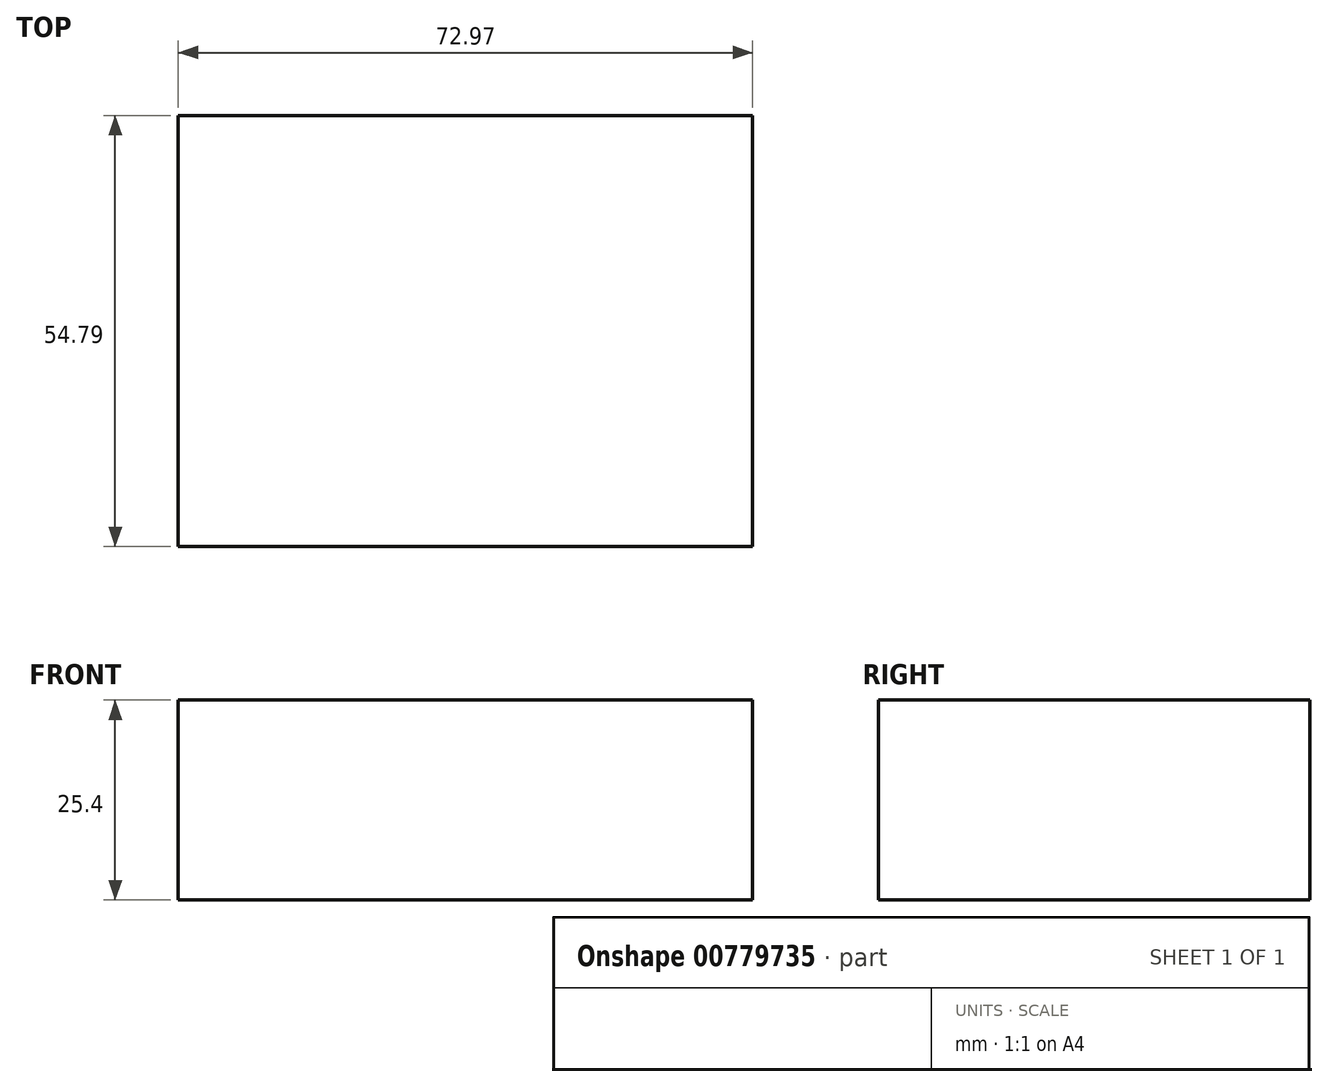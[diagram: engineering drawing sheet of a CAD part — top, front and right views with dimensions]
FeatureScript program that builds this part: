
annotation { "Feature Type Name" : "Feature", "Feature Type Description" : "" }
export const myFeature = defineFeature(function(context is Context, id is Id, definition is map)
    precondition{}
    {
        {
            var Q0;
            Q0=qCreatedBy(makeId("Top.planeOp"),FACE);
            var sketch = newSketch(context, id + "F0", { "sketchPlane" : qUnion([Q0])});
            skLineSegment(sketch, "E0.bottom", {"start": v(-33.76, 20.7) * mm, "end": v(39.21, 20.7) * mm});
            skLineSegment(sketch, "E0.top", {"start": v(-33.76, -34.1) * mm, "end": v(39.21, -34.1) * mm});
            skLineSegment(sketch, "E0.left", {"start": v(-33.76, 20.7) * mm, "end": v(-33.76, -34.1) * mm});
            skLineSegment(sketch, "E0.right", {"start": v(39.21, 20.7) * mm, "end": v(39.21, -34.1) * mm});
            skSolve(sketch);
        }
        {
            var Q0;
            Q0=makeQuery(id+"F0.imprint","IMPRINT",FACE,{"disambiguationData":[TD([[makeQuery(id+"F0.imprint","IMPRINT",EDGE,{"derivedFrom":sQuery(id+"F0.wireOp",EDGE,"E0.bottom")}),-1.0]])]});
            extrude(context, id + "F1", {"entities" : qUnion([Q0]), "depth" : 25.4 * mm, "offsetDistance" : 25.4 * mm});
        }
    });
